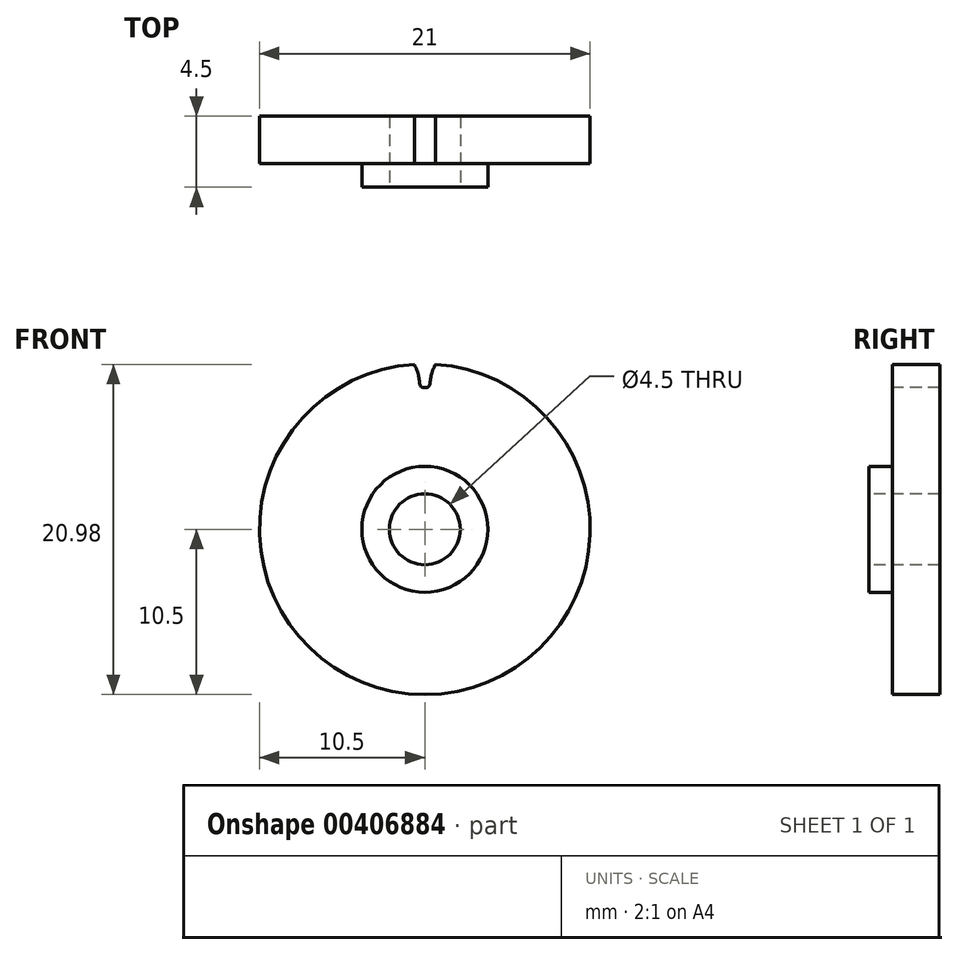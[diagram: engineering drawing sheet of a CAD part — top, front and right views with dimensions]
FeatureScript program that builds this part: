
annotation { "Feature Type Name" : "Feature", "Feature Type Description" : "" }
export const myFeature = defineFeature(function(context is Context, id is Id, definition is map)
    precondition{}
    {
        {
            var Q0;
            Q0=qCreatedBy(makeId("Front.planeOp"),FACE);
            var sketch = newSketch(context, id + "F0", { "sketchPlane" : qUnion([Q0])});
            skCircle(sketch, "E0", {"center": v(0, 0) * mm, "radius": 10.5 * mm});
            skSolve(sketch);
        }
        {
            var Q0;
            Q0 = qSketchRegion(id + "F0", true);
            extrude(context, id + "F1", {"entities" : qUnion([Q0]), "endBound" : BoundingType.SYMMETRIC, "depth" : 3 * mm});
        }
        {
            var Q0;
            Q0=makeQuery(id+"F1.opExtrude","CAP_FACE",FACE,{"disambiguationData":[OSD([sQuery(id+"F0.wireOp",EDGE,"E0")])],"isStart":false});
            var sketch = newSketch(context, id + "F2", { "sketchPlane" : qUnion([Q0])});
            skCircle(sketch, "E1", {"center": v(0, 0) * mm, "radius": 2.25 * mm});
            skCircle(sketch, "E2", {"center": v(0, 0) * mm, "radius": 4 * mm});
            skSolve(sketch);
        }
        {
            var Q0;
            Q0=makeQuery(id+"F2.imprint","IMPRINT",FACE,{"disambiguationData":[TD([[makeQuery(id+"F2.imprint","IMPRINT",EDGE,{"derivedFrom":sQuery(id+"F2.wireOp",EDGE,"E1")}),1.0]])]});
            extrude(context, id + "F3", {"entities" : qUnion([Q0]), "operationType" : NewBodyOperationType.REMOVE, "oppositeDirection" : true, "depth" : 25 * mm});
        }
        {
            var Q0;
            Q0=makeQuery(id+"F2.imprint","IMPRINT",FACE,{"disambiguationData":[TD([[makeQuery(id+"F2.imprint","IMPRINT",EDGE,{"derivedFrom":sQuery(id+"F2.wireOp",EDGE,"E1")}),-1.0]])]});
            extrude(context, id + "F4", {"entities" : qUnion([Q0]), "operationType" : NewBodyOperationType.ADD, "depth" : 1.5 * mm});
        }
        {
            var Q0;
            Q0=makeQuery(id+"F1.opExtrude","CAP_FACE",FACE,{"disambiguationData":[OSD([sQuery(id+"F0.wireOp",EDGE,"E0")])],"isStart":false});
            var sketch = newSketch(context, id + "F5", { "sketchPlane" : qUnion([Q0])});
            skLineSegment(sketch, "E3", {"start": v(-0.3, 9) * mm, "end": v(0.3, 9) * mm});
            skFitSpline(sketch, "E4", {"points": [v(-0.67, 10.48) * mm, v(-0.43, 9.88) * mm, v(-0.3, 9) * mm], "startDerivative": vector(0.58, -1.27) * mm, "endDerivative": vector(0.18, -1.72) * mm});
            skLineSegment(sketch, "E5", {"start": v(0, 9) * mm, "end": v(0, 10.4) * mm});
            skLineSegment(sketch, "E6", {"start": v(0, 0) * mm, "end": v(0, 12.68) * mm});
            skFitSpline(sketch, "E7.MirrorCS", {"points": [v(0.67, 10.48) * mm, v(0.43, 9.88) * mm, v(0.3, 9) * mm], "startDerivative": vector(-0.58, -1.27) * mm, "endDerivative": vector(-0.18, -1.72) * mm});
            skSolve(sketch);
        }
        {
            var Q0;
            {var subQ6=sQuery(id+"F5.wireOp",EDGE,"E4");Q0=makeQuery(id+"F5.imprint","IMPRINT",FACE,{"disambiguationData":[TD([[makeQuery(id+"F5.imprint","IMPRINT",EDGE,{"derivedFrom":subQ6}),1.0]])]});}
            var Q1;
            {var subQ0=sQuery(id+"F5.wireOp",EDGE,"E7.MirrorCS");Q1=makeQuery(id+"F5.imprint","IMPRINT",FACE,{"disambiguationData":[TD([[makeQuery(id+"F5.imprint","IMPRINT",EDGE,{"derivedFrom":subQ0}),-1.0]])]});}
            extrude(context, id + "F6", {"entities" : qUnion([Q0, Q1]), "operationType" : NewBodyOperationType.REMOVE, "oppositeDirection" : true, "depth" : 25 * mm});
        }
        {
            var Q0;
            Q0=makeQuery(id+"F6.boolean.opBoolean","COPY",EDGE,{"derivedFrom":makeQuery(id+"F6.opExtrude","SWEPT_EDGE",EDGE,{"disambiguationData":[OSD([sQuery(id+"F5.wireOp",EDGE,"E3"),sQuery(id+"F5.wireOp",EDGE,"PPkPAWcl-Al8R-jPHX-91Vw-yx1lCCYvdamm")])]})});
            var Q1;
            Q1=makeQuery(id+"F6.boolean.opBoolean","COPY",EDGE,{"derivedFrom":makeQuery(id+"F6.opExtrude","SWEPT_EDGE",EDGE,{"disambiguationData":[OSD([sQuery(id+"F5.wireOp",EDGE,"E3"),sQuery(id+"F5.wireOp",EDGE,"cADFVUA3-EMaD-w2mp-eGuG-jneyfjIeLrG9")])]})});
            fillet(context, id + "F7", {"entities" : qUnion([Q0, Q1]), "radius" : 0.22 * mm, "tangentPropagation" : true, "allowEdgeOverflow" : false});
        }
    });
